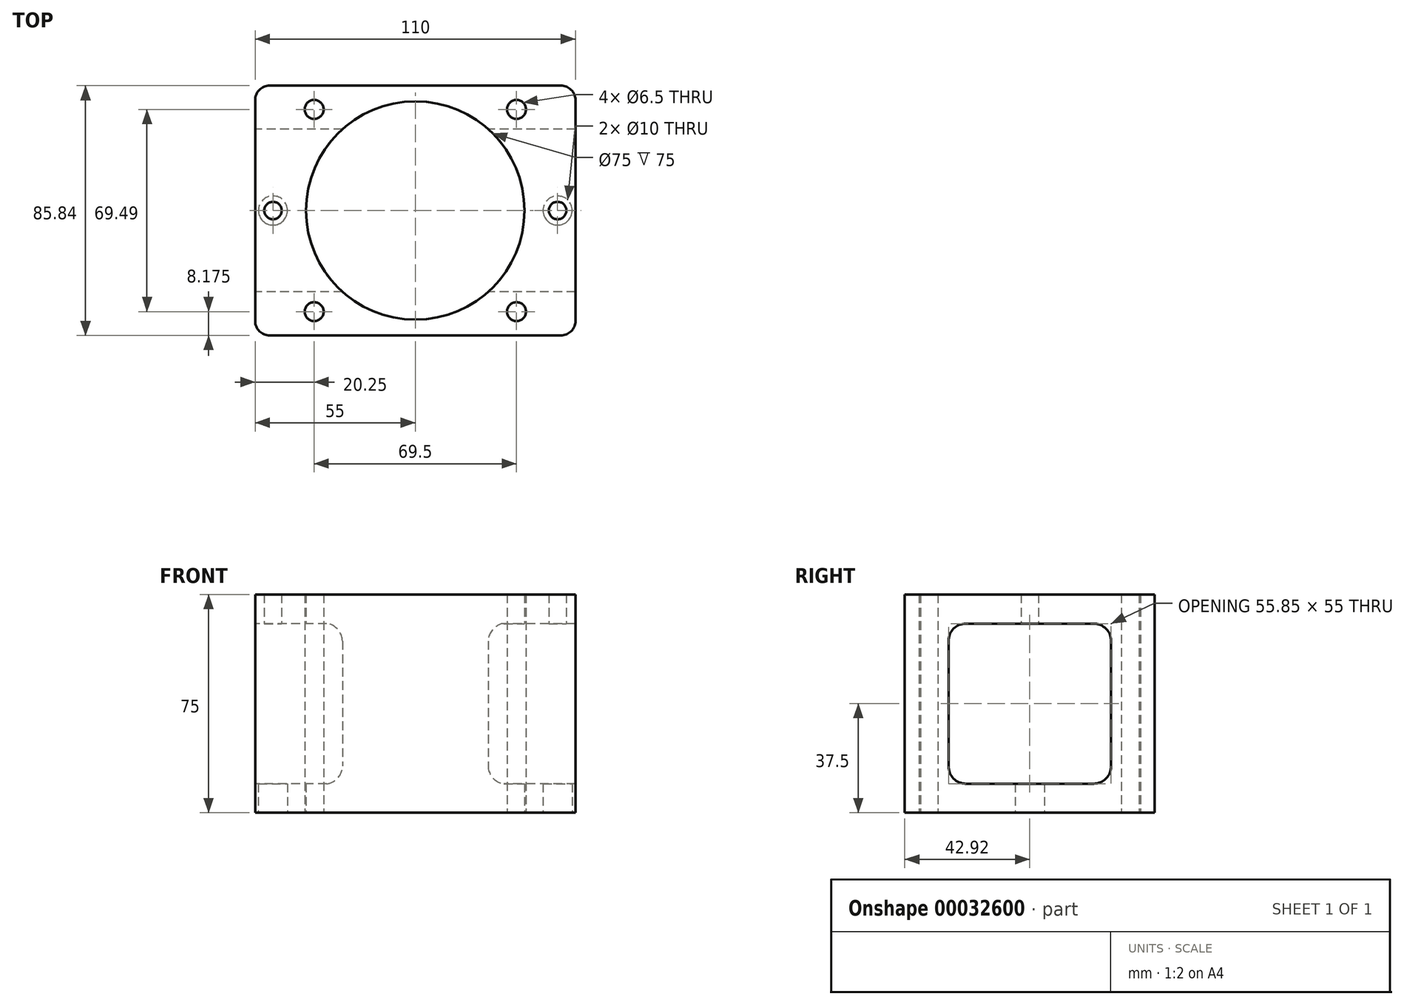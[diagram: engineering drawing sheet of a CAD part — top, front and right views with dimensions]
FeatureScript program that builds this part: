
annotation { "Feature Type Name" : "Feature", "Feature Type Description" : "" }
export const myFeature = defineFeature(function(context is Context, id is Id, definition is map)
    precondition{}
    {
        {
            var Q0;
            Q0=qCreatedBy(makeId("Top.planeOp"),FACE);
            var sketch = newSketch(context, id + "F0", { "sketchPlane" : qUnion([Q0])});
            skLineSegment(sketch, "E0.rect.bottom", {"start": v(-50, 42.93) * mm, "end": v(50, 42.93) * mm});
            skLineSegment(sketch, "E0.rect.top", {"start": v(-50, -42.93) * mm, "end": v(50, -42.93) * mm});
            skLineSegment(sketch, "E0.rect.left", {"start": v(-55, 37.93) * mm, "end": v(-55, -37.93) * mm});
            skLineSegment(sketch, "E0.rect.right", {"start": v(55, 37.93) * mm, "end": v(55, -37.93) * mm});
            skPoint(sketch, "E0.rect.middle", {"position": v(0, 0) * mm});
            skCircle(sketch, "E1", {"center": v(0, 0) * mm, "radius": 37.5 * mm});
            skCircle(sketch, "E2", {"center": v(-48.88, 0) * mm, "radius": 5 * mm});
            skCircle(sketch, "E3", {"center": v(48.87, 0) * mm, "radius": 5 * mm});
            skCircle(sketch, "E4", {"center": v(-34.75, 34.75) * mm, "radius": 3.25 * mm});
            skCircle(sketch, "E5", {"center": v(-34.75, -34.75) * mm, "radius": 3.25 * mm});
            skCircle(sketch, "E6", {"center": v(34.75, 34.75) * mm, "radius": 3.25 * mm});
            skCircle(sketch, "E7", {"center": v(34.75, -34.75) * mm, "radius": 3.25 * mm});
            skPoint(sketch, "E8.visualSharp", {"position": v(-55, 42.93) * mm});
            skArc(sketch, "E8.filletArc", {"start": v(-50, 42.93) * mm, "mid": v(-53.54, 41.46) * mm, "end": v(-55, 37.93) * mm});
            skPoint(sketch, "E9.visualSharp", {"position": v(55, 42.93) * mm});
            skArc(sketch, "E9.filletArc", {"start": v(55, 37.93) * mm, "mid": v(53.54, 41.46) * mm, "end": v(50, 42.92) * mm});
            skPoint(sketch, "E10.visualSharp", {"position": v(55, -42.93) * mm});
            skArc(sketch, "E10.filletArc", {"start": v(50, -42.93) * mm, "mid": v(53.54, -41.46) * mm, "end": v(55, -37.93) * mm});
            skPoint(sketch, "E11.visualSharp", {"position": v(-55, -42.93) * mm});
            skArc(sketch, "E11.filletArc", {"start": v(-55, -37.93) * mm, "mid": v(-53.54, -41.46) * mm, "end": v(-50, -42.93) * mm});
            skCircle(sketch, "E12", {"center": v(48.87, 0) * mm, "radius": 3 * mm});
            skCircle(sketch, "E13", {"center": v(-48.88, 0) * mm, "radius": 3 * mm});
            skSolve(sketch);
        }
        {
            var Q0;
            Q0=makeQuery(id+"F0.imprint","IMPRINT",FACE,{"disambiguationData":[TD([[makeQuery(id+"F0.imprint","IMPRINT",EDGE,{"derivedFrom":sQuery(id+"F0.wireOp",EDGE,"E0.rect.bottom")}),-1.0]])]});
            var Q1;
            Q1=makeQuery(id+"F0.imprint","IMPRINT",FACE,{"disambiguationData":[TD([[makeQuery(id+"F0.imprint","IMPRINT",EDGE,{"derivedFrom":sQuery(id+"F0.wireOp",EDGE,"E3")}),1.0]])]});
            var Q2;
            Q2=makeQuery(id+"F0.imprint","IMPRINT",FACE,{"disambiguationData":[TD([[makeQuery(id+"F0.imprint","IMPRINT",EDGE,{"derivedFrom":sQuery(id+"F0.wireOp",EDGE,"E2")}),1.0]])]});
            extrude(context, id + "F1", {"entities" : qUnion([Q0, Q1, Q2]), "depth" : 75 * mm});
        }
        {
            var Q0;
            Q0=makeQuery(id+"F1.opExtrude","SWEPT_FACE",FACE,{"disambiguationData":[OSD([sQuery(id+"F0.wireOp",EDGE,"E0.rect.left")])]});
            var sketch = newSketch(context, id + "F2", { "sketchPlane" : qUnion([Q0])});
            skLineSegment(sketch, "E14.rect.bottom", {"start": v(-21.93, 65) * mm, "end": v(21.93, 65) * mm});
            skLineSegment(sketch, "E14.rect.top", {"start": v(-21.93, 10) * mm, "end": v(21.93, 10) * mm});
            skLineSegment(sketch, "E14.rect.left", {"start": v(-27.93, 59) * mm, "end": v(-27.93, 16) * mm});
            skLineSegment(sketch, "E14.rect.right", {"start": v(27.93, 59) * mm, "end": v(27.93, 16) * mm});
            skPoint(sketch, "E14.rect.middle", {"position": v(0, 37.5) * mm});
            skPoint(sketch, "E15.visualSharp", {"position": v(-27.93, 65) * mm});
            skArc(sketch, "E15.filletArc", {"start": v(-21.93, 65) * mm, "mid": v(-26.17, 63.24) * mm, "end": v(-27.93, 59) * mm});
            skPoint(sketch, "E16.visualSharp", {"position": v(27.93, 65) * mm});
            skArc(sketch, "E16.filletArc", {"start": v(27.92, 59) * mm, "mid": v(26.17, 63.24) * mm, "end": v(21.93, 65) * mm});
            skPoint(sketch, "E17.visualSharp", {"position": v(27.93, 10) * mm});
            skArc(sketch, "E17.filletArc", {"start": v(21.93, 10) * mm, "mid": v(26.17, 11.76) * mm, "end": v(27.93, 16) * mm});
            skPoint(sketch, "E18.visualSharp", {"position": v(-27.93, 10) * mm});
            skArc(sketch, "E18.filletArc", {"start": v(-27.93, 16) * mm, "mid": v(-26.17, 11.76) * mm, "end": v(-21.93, 10) * mm});
            skSolve(sketch);
        }
        {
            var Q0;
            Q0=makeQuery(id+"F2.imprint","IMPRINT",FACE,{"disambiguationData":[TD([[makeQuery(id+"F2.imprint","IMPRINT",EDGE,{"derivedFrom":sQuery(id+"F2.wireOp",EDGE,"E14.rect.bottom")}),-1.0]])]});
            extrude(context, id + "F3", {"entities" : qUnion([Q0]), "operationType" : NewBodyOperationType.REMOVE, "oppositeDirection" : true, "depth" : 129.52 * mm, "hasSecondDirection" : true, "secondDirectionOppositeDirection" : false, "secondDirectionDepth" : 58.36 * mm});
        }
        {
            var Q0;
            Q0=makeQuery(id+"F0.imprint","IMPRINT",FACE,{"disambiguationData":[TD([[makeQuery(id+"F0.imprint","IMPRINT",EDGE,{"derivedFrom":sQuery(id+"F0.wireOp",EDGE,"E2")}),1.0]])]});
            var Q1;
            Q1=makeQuery(id+"F0.imprint","IMPRINT",FACE,{"disambiguationData":[TD([[makeQuery(id+"F0.imprint","IMPRINT",EDGE,{"derivedFrom":sQuery(id+"F0.wireOp",EDGE,"E3")}),1.0]])]});
            extrude(context, id + "F4", {"entities" : qUnion([Q0, Q1]), "operationType" : NewBodyOperationType.REMOVE, "depth" : 40.7 * mm});
        }
    });
